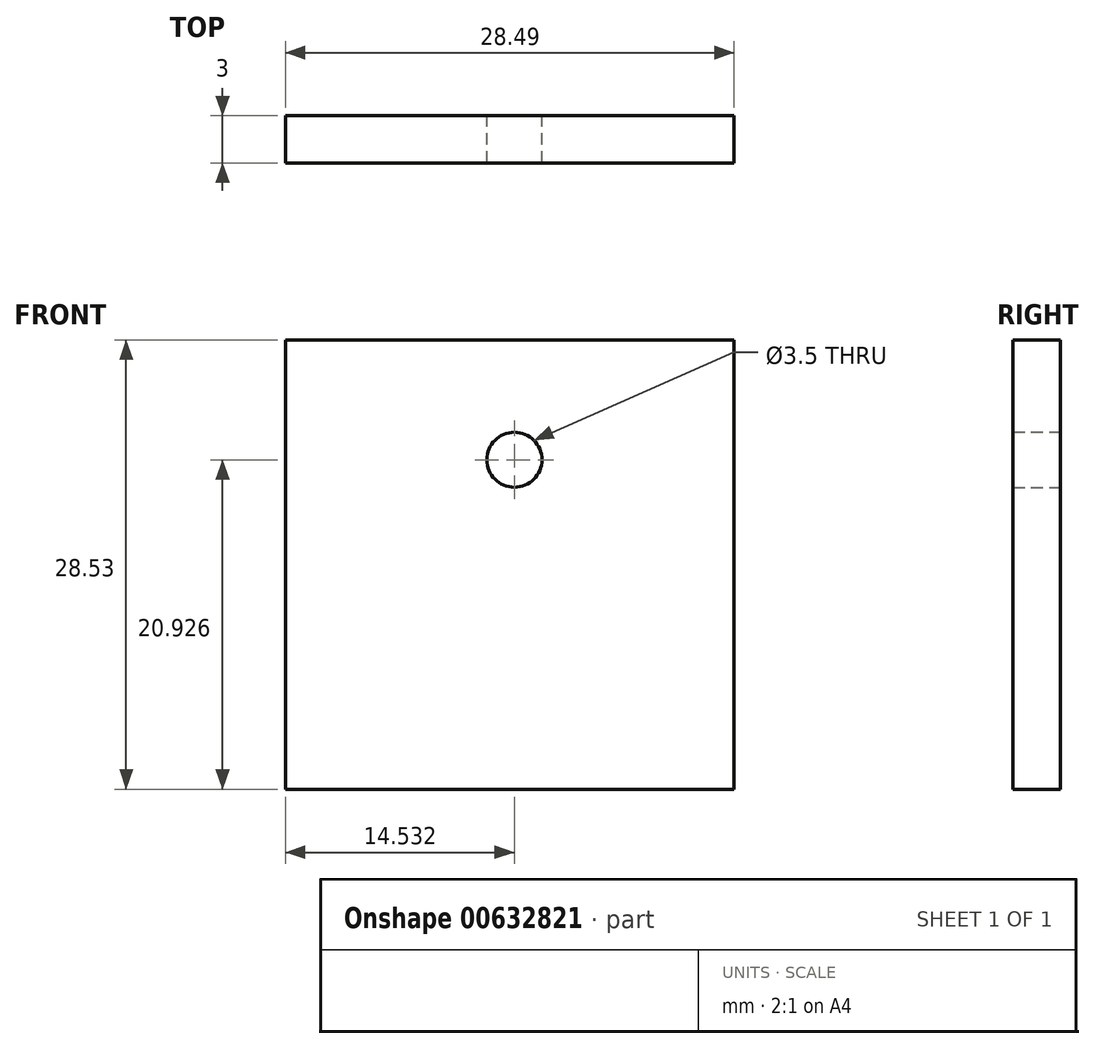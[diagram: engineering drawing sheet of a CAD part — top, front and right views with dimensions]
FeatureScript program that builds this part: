
annotation { "Feature Type Name" : "Feature", "Feature Type Description" : "" }
export const myFeature = defineFeature(function(context is Context, id is Id, definition is map)
    precondition{}
    {
        {
            var Q0;
            Q0=qCreatedBy(makeId("Front.planeOp"),FACE);
            var sketch = newSketch(context, id + "F0", { "sketchPlane" : qUnion([Q0])});
            skLineSegment(sketch, "E0.bottom", {"start": v(0, 0) * mm, "end": v(28.49, 0) * mm});
            skLineSegment(sketch, "E0.top", {"start": v(0, 28.53) * mm, "end": v(28.49, 28.53) * mm});
            skLineSegment(sketch, "E0.left", {"start": v(0, 0) * mm, "end": v(0, 28.53) * mm});
            skLineSegment(sketch, "E0.right", {"start": v(28.49, 0) * mm, "end": v(28.49, 28.53) * mm});
            skCircle(sketch, "E1", {"center": v(14.53, 20.93) * mm, "radius": 1.75 * mm});
            skSolve(sketch);
        }
        {
            var Q0;
            Q0 = qSketchRegion(id + "F0", true);
            extrude(context, id + "F1", {"entities" : qUnion([Q0]), "depth" : 3 * mm, "offsetDistance" : 25 * mm});
        }
    });
